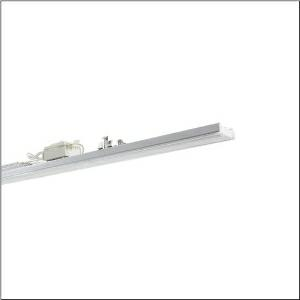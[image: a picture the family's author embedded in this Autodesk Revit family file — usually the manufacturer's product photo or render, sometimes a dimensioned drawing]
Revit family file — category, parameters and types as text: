
# Revit family: licross_r__11_recessed_extreme_mo_51te18dn485ge_7b54
name_source: partatom
category: Lighting Fixtures
units: mm (PartAtom-declared; Revit-internal decimal feet)

## family parameters
Cut with Voids When Loaded = No
Host = Face
Light Source = No
Part Type = Normal
Room Calculation Point = No
Round Connector Dimension = Use Diameter
Shared = No

## types (1)
- --- (1 x LED, 8910 lm, 50.3 W, 4000K)
    Apparent Load = 50 VA
    CIE Flux Codes = 83 96 99 100 100
    Color Rendering = 80
    Color Temperature = 4000K
    Default Elevation = 1800 mm
    Description = Licross® 11 Recessed extreme MO, luminaire insert, of sheet steel, galvanised, coil coated, white, length: 1.500mm, width: 66mm, height: 67mm, LED rated luminous flux: 8.910lm, light colour: 840, control gear: DALI 2, with plug, 5-pole, with phase selection, mains connection: 220..240V, AC, 50/60Hz, rated input power: 50W, halogen-free wiring, primary light control with lens, of plastic, primary optical cover: cover, of PMMA, light emission: direct distribution, primary light characteristic: symmetric, protection rating (complete): IP54, insulation class (complete): insulation class I (protective earthing), certification: CE, ENEC, VDE, UKCA, protection symbol: D if used in an environment with non-conductive dust loads with corresponding accessories, impact resistance: IK06, permissible ambient temperature for indoor applications: -25..+45°C, corresponds to IFS (International Featured Standards) requirements for safety and quality in the food industry, reducing of maximum allowable ambient temperature of 5°C with ceiling mounting, LABS conformity tested according to VDMA 24364:2018-05, packaging unit: 1 piece
    Height = 58 mm
    Lamp = 1 x LED
    Lamp Light Flux = 8910 lm
    Lamp Power = 50.3 W
    Lamp count = 1
    Length = 1500 mm
    Luminous efficacy = 177 lm/W
    Manufacturer = Siteco
    ModVariant = No
    Model = 51TE18DN485GE
    Mounting Place = Ceiling
    Mounting Type = Pendant
    Number of Poles = 1
    OnlyDefault = Yes
    Power Factor = 1
    Product Name = Licross® 11 Recessed extreme MO
    Product group = luminaire insert
    ProductGroupID = 902
    Protection Class = Protection class I
    Protection Degree = IP 54
    RLX_Detail_Level = 1
    RLX_Emergency_Light_Flux = 0 lm
    RLX_Emergency_Type = 0
    RLX_Emergency_Type_DB = No
    RlxData = <blob elided: 24633 chars, md5=3d6d054b>
    Socket = socket
    Standby Power = 0 W
    System Light Flux = 8910 lm
    System Power = 50 W
    Type Comments = factory setting: luminous flux: 100 % | dim-lin: 254 | 335 mA
    Type Image = l_1296930.jpg
    URL = http://relux.com
    VarID = @adj_089740
    Voltage = 0 V
    Weight = 0.00 kg
    Width = 66 mm

## geometry (parser evidence)
native form markers: Blend x4, Sweep x12
no freeform markers — native parametric forms only
